# Revit family: QF_Vivreau_Waste Water Container
name_source: partatom
category: Specialty Equipment
revit_build: Autodesk Revit 2018 (Build: 20190510_1515(x64)
units: mm (PartAtom-declared; Revit-internal decimal feet)

## family parameters
Always vertical = Yes
Cut with Voids When Loaded = No
OmniClass Number = 23.40.40.14.24
OmniClass Title = Food Dispensing Equipment
Part Type = Normal
Room Calculation Point = No
Round Connector Dimension = Use Diameter
Shared = No
Work Plane-Based = No

## types (1)
- QF_Vivreau_Waste Water Container
    Assembly Code = E1090320
    CSI MasterFormat = 11 46 00
    Depth = 0' - 7 9/16"
    Description = Waste Water Container
    Foodservice Equipment Identifier = Yes
    Height = 0' - 10 1/4"
    Identify Quantity as Lot = Yes
    Manufacturer = Vivreau Advanced Water Systems
    Masterspec = Division 11
    Model = Waste Water Container
    Specification by Manufacturer = (1041216) Sensor controlled waste water container
    URL = https://vivreauwater.com
    Weight in Pounds = 1
    Width = 0' - 5 21/32"

## geometry (parser evidence)
native form markers: Sweep x2
no freeform markers — native parametric forms only
